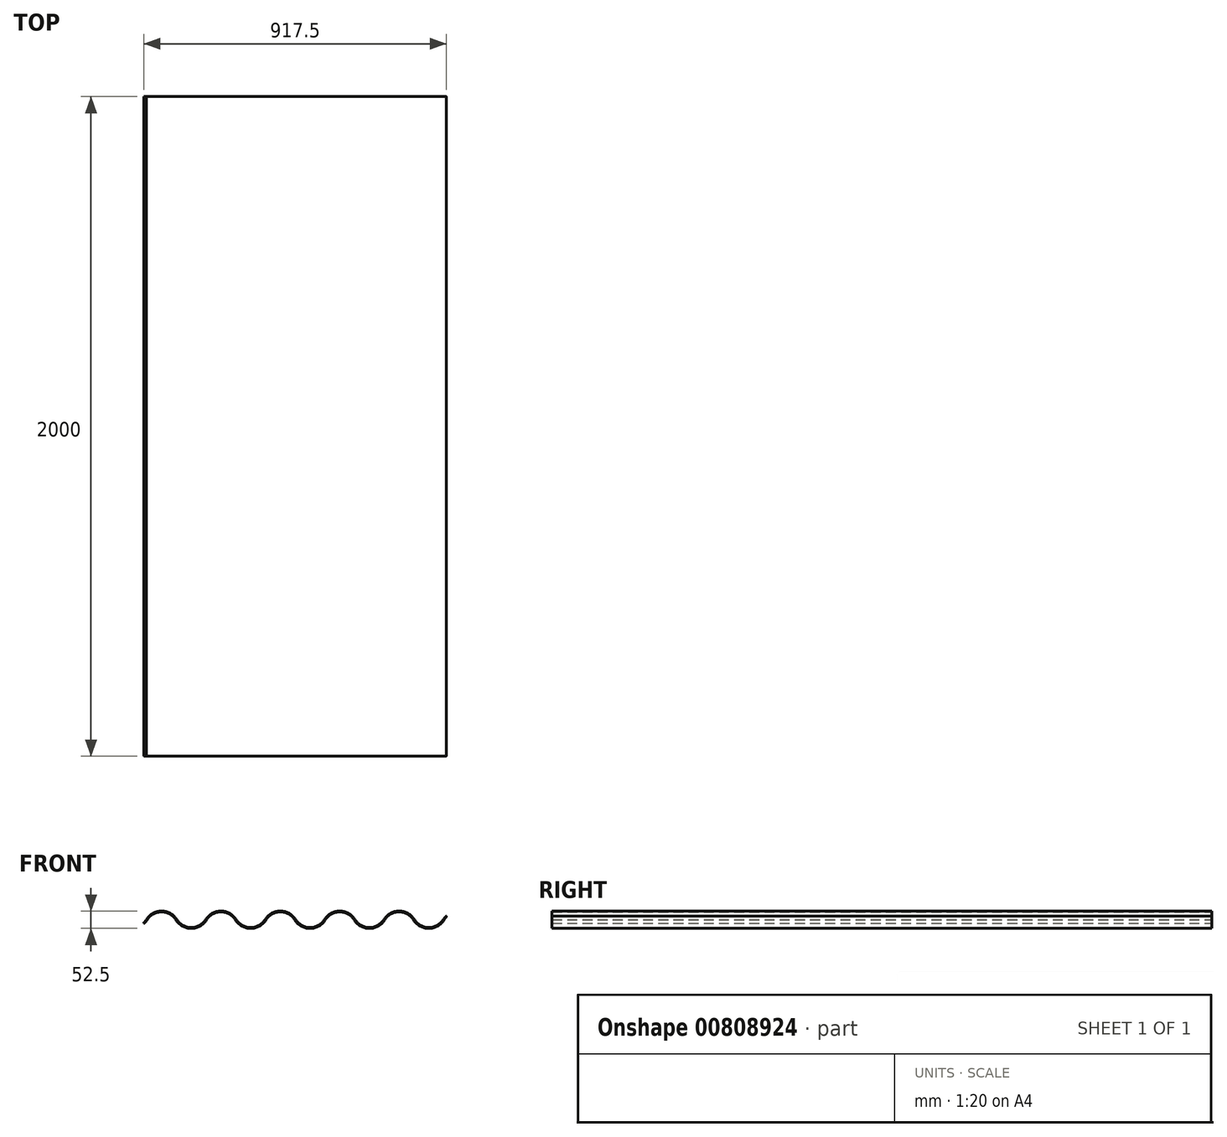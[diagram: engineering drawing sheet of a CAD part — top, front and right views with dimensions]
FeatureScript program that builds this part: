
annotation { "Feature Type Name" : "Feature", "Feature Type Description" : "" }
export const myFeature = defineFeature(function(context is Context, id is Id, definition is map)
    precondition{}
    {
        {
            var Q0;
            Q0=qCreatedBy(makeId("Front.planeOp"),FACE);
            var sketch = newSketch(context, id + "F0", { "sketchPlane" : qUnion([Q0])});
            skArc(sketch, "E0", {"start": v(0, 0) * mm, "mid": v(-45, 25) * mm, "end": v(-90, 0) * mm});
            skArc(sketch, "E1", {"start": v(0, 0) * mm, "mid": v(45, -25) * mm, "end": v(90, 0) * mm});
            skArc(sketch, "E2.1.0.0", {"start": v(180, 0) * mm, "mid": v(135, 25) * mm, "end": v(90, 0) * mm});
            skArc(sketch, "E2.1.0.1", {"start": v(180, 0) * mm, "mid": v(135, 25) * mm, "end": v(90, 0) * mm});
            skArc(sketch, "E2.1.0.2", {"start": v(180, 0) * mm, "mid": v(225, -25) * mm, "end": v(270, 0) * mm});
            skArc(sketch, "E2.2.0.0", {"start": v(360, 0) * mm, "mid": v(315, 25) * mm, "end": v(270, 0) * mm});
            skArc(sketch, "E2.2.0.1", {"start": v(360, 0) * mm, "mid": v(315, 25) * mm, "end": v(270, 0) * mm});
            skArc(sketch, "E2.2.0.2", {"start": v(360, 0) * mm, "mid": v(405, -25) * mm, "end": v(450, 0) * mm});
            skArc(sketch, "E2.3.0.0", {"start": v(540, 0) * mm, "mid": v(495, 25) * mm, "end": v(450, 0) * mm});
            skArc(sketch, "E2.3.0.1", {"start": v(540, 0) * mm, "mid": v(495, 25) * mm, "end": v(450, 0) * mm});
            skArc(sketch, "E2.3.0.2", {"start": v(540, 0) * mm, "mid": v(585, -25) * mm, "end": v(630, 0) * mm});
            skArc(sketch, "E2.4.0.0", {"start": v(720, 0) * mm, "mid": v(675, 25) * mm, "end": v(630, 0) * mm});
            skArc(sketch, "E2.4.0.1", {"start": v(720, 0) * mm, "mid": v(675, 25) * mm, "end": v(630, 0) * mm});
            skArc(sketch, "E2.4.0.2", {"start": v(720, 0) * mm, "mid": v(765, -25) * mm, "end": v(810, 0) * mm});
            skArc(sketch, "E3", {"start": v(-97.5, -9.45) * mm, "mid": v(-93.48, -4.94) * mm, "end": v(-90, 0) * mm});
            skArc(sketch, "E4.MirrorCS", {"start": v(810, 0) * mm, "mid": v(813.48, 4.94) * mm, "end": v(817.5, 9.45) * mm});
            skPoint(sketch, "E5.orphan", {"position": v(900, 0) * mm});
            skArc(sketch, "E6.0.startCap", {"start": v(181.06, 0.66) * mm, "mid": v(180.66, -1.06) * mm, "end": v(178.94, -0.66) * mm});
            skArc(sketch, "E6.0.endCap", {"start": v(91.06, -0.66) * mm, "mid": v(89.34, -1.06) * mm, "end": v(88.94, 0.66) * mm});
            skArc(sketch, "E6.0.left", {"start": v(178.94, -0.66) * mm, "mid": v(135, 23.75) * mm, "end": v(91.06, -0.66) * mm});
            skArc(sketch, "E6.0.right", {"start": v(181.06, 0.66) * mm, "mid": v(135, 26.25) * mm, "end": v(88.94, 0.66) * mm});
            skArc(sketch, "E6.1.startCap", {"start": v(178.94, -0.66) * mm, "mid": v(179.34, 1.06) * mm, "end": v(181.06, 0.66) * mm});
            skArc(sketch, "E6.1.endCap", {"start": v(268.94, 0.66) * mm, "mid": v(270.66, 1.06) * mm, "end": v(271.06, -0.66) * mm});
            skArc(sketch, "E6.1.left", {"start": v(181.06, 0.66) * mm, "mid": v(225, -23.75) * mm, "end": v(268.94, 0.66) * mm});
            skArc(sketch, "E6.1.right", {"start": v(178.94, -0.66) * mm, "mid": v(225, -26.25) * mm, "end": v(271.06, -0.66) * mm});
            skArc(sketch, "E6.2.startCap", {"start": v(-1.06, -0.66) * mm, "mid": v(-0.66, 1.06) * mm, "end": v(1.06, 0.66) * mm});
            skArc(sketch, "E6.2.endCap", {"start": v(88.94, 0.66) * mm, "mid": v(90.66, 1.06) * mm, "end": v(91.06, -0.66) * mm});
            skArc(sketch, "E6.2.left", {"start": v(1.06, 0.66) * mm, "mid": v(45, -23.75) * mm, "end": v(88.94, 0.66) * mm});
            skArc(sketch, "E6.2.right", {"start": v(-1.06, -0.66) * mm, "mid": v(45, -26.25) * mm, "end": v(91.06, -0.66) * mm});
            skArc(sketch, "E6.3.startCap", {"start": v(538.94, -0.66) * mm, "mid": v(539.34, 1.06) * mm, "end": v(541.06, 0.66) * mm});
            skArc(sketch, "E6.3.endCap", {"start": v(628.94, 0.66) * mm, "mid": v(630.66, 1.06) * mm, "end": v(631.06, -0.66) * mm});
            skArc(sketch, "E6.3.left", {"start": v(541.06, 0.66) * mm, "mid": v(585, -23.75) * mm, "end": v(628.94, 0.66) * mm});
            skArc(sketch, "E6.3.right", {"start": v(538.94, -0.66) * mm, "mid": v(585, -26.25) * mm, "end": v(631.06, -0.66) * mm});
            skArc(sketch, "E6.4.startCap", {"start": v(718.94, -0.66) * mm, "mid": v(719.34, 1.06) * mm, "end": v(721.06, 0.66) * mm});
            skArc(sketch, "E6.4.endCap", {"start": v(808.94, 0.66) * mm, "mid": v(810.66, 1.06) * mm, "end": v(811.06, -0.66) * mm});
            skArc(sketch, "E6.4.left", {"start": v(721.06, 0.66) * mm, "mid": v(765, -23.75) * mm, "end": v(808.94, 0.66) * mm});
            skArc(sketch, "E6.4.right", {"start": v(718.94, -0.66) * mm, "mid": v(765, -26.25) * mm, "end": v(811.06, -0.66) * mm});
            skArc(sketch, "E6.5.startCap", {"start": v(541.06, 0.66) * mm, "mid": v(540.66, -1.06) * mm, "end": v(538.94, -0.66) * mm});
            skArc(sketch, "E6.5.endCap", {"start": v(451.06, -0.66) * mm, "mid": v(449.34, -1.06) * mm, "end": v(448.94, 0.66) * mm});
            skArc(sketch, "E6.5.left", {"start": v(538.94, -0.66) * mm, "mid": v(495, 23.75) * mm, "end": v(451.06, -0.66) * mm});
            skArc(sketch, "E6.5.right", {"start": v(541.06, 0.66) * mm, "mid": v(495, 26.25) * mm, "end": v(448.94, 0.66) * mm});
            skArc(sketch, "E6.6.startCap", {"start": v(-96.62, -10.34) * mm, "mid": v(-98.38, -10.34) * mm, "end": v(-98.38, -8.57) * mm});
            skArc(sketch, "E6.6.endCap", {"start": v(-91.06, 0.66) * mm, "mid": v(-89.34, 1.06) * mm, "end": v(-88.94, -0.66) * mm});
            skArc(sketch, "E6.6.left", {"start": v(-98.38, -8.57) * mm, "mid": v(-94.46, -4.16) * mm, "end": v(-91.06, 0.66) * mm});
            skArc(sketch, "E6.6.right", {"start": v(-96.62, -10.34) * mm, "mid": v(-92.5, -5.72) * mm, "end": v(-88.94, -0.66) * mm});
            skArc(sketch, "E6.7.startCap", {"start": v(1.06, 0.66) * mm, "mid": v(0.66, -1.06) * mm, "end": v(-1.06, -0.66) * mm});
            skArc(sketch, "E6.7.endCap", {"start": v(-88.94, -0.66) * mm, "mid": v(-90.66, -1.06) * mm, "end": v(-91.06, 0.66) * mm});
            skArc(sketch, "E6.7.left", {"start": v(-1.06, -0.66) * mm, "mid": v(-45, 23.75) * mm, "end": v(-88.94, -0.66) * mm});
            skArc(sketch, "E6.7.right", {"start": v(1.06, 0.66) * mm, "mid": v(-45, 26.25) * mm, "end": v(-91.06, 0.66) * mm});
            skArc(sketch, "E6.8.startCap", {"start": v(721.06, 0.66) * mm, "mid": v(720.66, -1.06) * mm, "end": v(718.94, -0.66) * mm});
            skArc(sketch, "E6.8.endCap", {"start": v(631.06, -0.66) * mm, "mid": v(629.34, -1.06) * mm, "end": v(628.94, 0.66) * mm});
            skArc(sketch, "E6.8.left", {"start": v(718.94, -0.66) * mm, "mid": v(675, 23.75) * mm, "end": v(631.06, -0.66) * mm});
            skArc(sketch, "E6.8.right", {"start": v(721.06, 0.66) * mm, "mid": v(675, 26.25) * mm, "end": v(628.94, 0.66) * mm});
            skArc(sketch, "E6.9.startCap", {"start": v(811.06, -0.66) * mm, "mid": v(809.34, -1.06) * mm, "end": v(808.94, 0.66) * mm});
            skArc(sketch, "E6.9.endCap", {"start": v(816.62, 10.34) * mm, "mid": v(818.38, 10.34) * mm, "end": v(818.38, 8.57) * mm});
            skArc(sketch, "E6.9.left", {"start": v(808.94, 0.66) * mm, "mid": v(812.5, 5.72) * mm, "end": v(816.62, 10.34) * mm});
            skArc(sketch, "E6.9.right", {"start": v(811.06, -0.66) * mm, "mid": v(814.46, 4.16) * mm, "end": v(818.38, 8.57) * mm});
            skArc(sketch, "E6.10.startCap", {"start": v(358.94, -0.66) * mm, "mid": v(359.34, 1.06) * mm, "end": v(361.06, 0.66) * mm});
            skArc(sketch, "E6.10.endCap", {"start": v(448.94, 0.66) * mm, "mid": v(450.66, 1.06) * mm, "end": v(451.06, -0.66) * mm});
            skArc(sketch, "E6.10.left", {"start": v(361.06, 0.66) * mm, "mid": v(405, -23.75) * mm, "end": v(448.94, 0.66) * mm});
            skArc(sketch, "E6.10.right", {"start": v(358.94, -0.66) * mm, "mid": v(405, -26.25) * mm, "end": v(451.06, -0.66) * mm});
            skArc(sketch, "E6.11.startCap", {"start": v(361.06, 0.66) * mm, "mid": v(360.66, -1.06) * mm, "end": v(358.94, -0.66) * mm});
            skArc(sketch, "E6.11.endCap", {"start": v(271.06, -0.66) * mm, "mid": v(269.34, -1.06) * mm, "end": v(268.94, 0.66) * mm});
            skArc(sketch, "E6.11.left", {"start": v(358.94, -0.66) * mm, "mid": v(315, 23.75) * mm, "end": v(271.06, -0.66) * mm});
            skArc(sketch, "E6.11.right", {"start": v(361.06, 0.66) * mm, "mid": v(315, 26.25) * mm, "end": v(268.94, 0.66) * mm});
            skArc(sketch, "E6.12.startCap", {"start": v(-1.06, -0.66) * mm, "mid": v(-0.66, 1.06) * mm, "end": v(1.06, 0.66) * mm});
            skArc(sketch, "E6.12.endCap", {"start": v(88.94, 0.66) * mm, "mid": v(90.66, 1.06) * mm, "end": v(91.06, -0.66) * mm});
            skArc(sketch, "E6.12.left", {"start": v(1.06, 0.66) * mm, "mid": v(45, -23.75) * mm, "end": v(88.94, 0.66) * mm});
            skArc(sketch, "E6.12.right", {"start": v(-1.06, -0.66) * mm, "mid": v(45, -26.25) * mm, "end": v(91.06, -0.66) * mm});
            skArc(sketch, "E6.13.startCap", {"start": v(181.06, 0.66) * mm, "mid": v(180.66, -1.06) * mm, "end": v(178.94, -0.66) * mm});
            skArc(sketch, "E6.13.endCap", {"start": v(91.06, -0.66) * mm, "mid": v(89.34, -1.06) * mm, "end": v(88.94, 0.66) * mm});
            skArc(sketch, "E6.13.left", {"start": v(178.94, -0.66) * mm, "mid": v(135, 23.75) * mm, "end": v(91.06, -0.66) * mm});
            skArc(sketch, "E6.13.right", {"start": v(181.06, 0.66) * mm, "mid": v(135, 26.25) * mm, "end": v(88.94, 0.66) * mm});
            skArc(sketch, "E6.14.startCap", {"start": v(1.06, 0.66) * mm, "mid": v(0.66, -1.06) * mm, "end": v(-1.06, -0.66) * mm});
            skArc(sketch, "E6.14.endCap", {"start": v(-88.94, -0.66) * mm, "mid": v(-90.66, -1.06) * mm, "end": v(-91.06, 0.66) * mm});
            skArc(sketch, "E6.14.left", {"start": v(-1.06, -0.66) * mm, "mid": v(-45, 23.75) * mm, "end": v(-88.94, -0.66) * mm});
            skArc(sketch, "E6.14.right", {"start": v(1.06, 0.66) * mm, "mid": v(-45, 26.25) * mm, "end": v(-91.06, 0.66) * mm});
            skArc(sketch, "E6.15.startCap", {"start": v(541.06, 0.66) * mm, "mid": v(540.66, -1.06) * mm, "end": v(538.94, -0.66) * mm});
            skArc(sketch, "E6.15.endCap", {"start": v(451.06, -0.66) * mm, "mid": v(449.34, -1.06) * mm, "end": v(448.94, 0.66) * mm});
            skArc(sketch, "E6.15.left", {"start": v(538.94, -0.66) * mm, "mid": v(495, 23.75) * mm, "end": v(451.06, -0.66) * mm});
            skArc(sketch, "E6.15.right", {"start": v(541.06, 0.66) * mm, "mid": v(495, 26.25) * mm, "end": v(448.94, 0.66) * mm});
            skArc(sketch, "E6.16.startCap", {"start": v(721.06, 0.66) * mm, "mid": v(720.66, -1.06) * mm, "end": v(718.94, -0.66) * mm});
            skArc(sketch, "E6.16.endCap", {"start": v(631.06, -0.66) * mm, "mid": v(629.34, -1.06) * mm, "end": v(628.94, 0.66) * mm});
            skArc(sketch, "E6.16.left", {"start": v(718.94, -0.66) * mm, "mid": v(675, 23.75) * mm, "end": v(631.06, -0.66) * mm});
            skArc(sketch, "E6.16.right", {"start": v(721.06, 0.66) * mm, "mid": v(675, 26.25) * mm, "end": v(628.94, 0.66) * mm});
            skArc(sketch, "E6.17.startCap", {"start": v(361.06, 0.66) * mm, "mid": v(360.66, -1.06) * mm, "end": v(358.94, -0.66) * mm});
            skArc(sketch, "E6.17.endCap", {"start": v(271.06, -0.66) * mm, "mid": v(269.34, -1.06) * mm, "end": v(268.94, 0.66) * mm});
            skArc(sketch, "E6.17.left", {"start": v(358.94, -0.66) * mm, "mid": v(315, 23.75) * mm, "end": v(271.06, -0.66) * mm});
            skArc(sketch, "E6.17.right", {"start": v(361.06, 0.66) * mm, "mid": v(315, 26.25) * mm, "end": v(268.94, 0.66) * mm});
            skSolve(sketch);
        }
        {
            var Q0;
            Q0 = qSketchRegion(id + "F0", true);
            extrude(context, id + "F1", {"entities" : qUnion([Q0]), "depth" : 2000 * mm, "offsetDistance" : 25 * mm});
        }
    });
